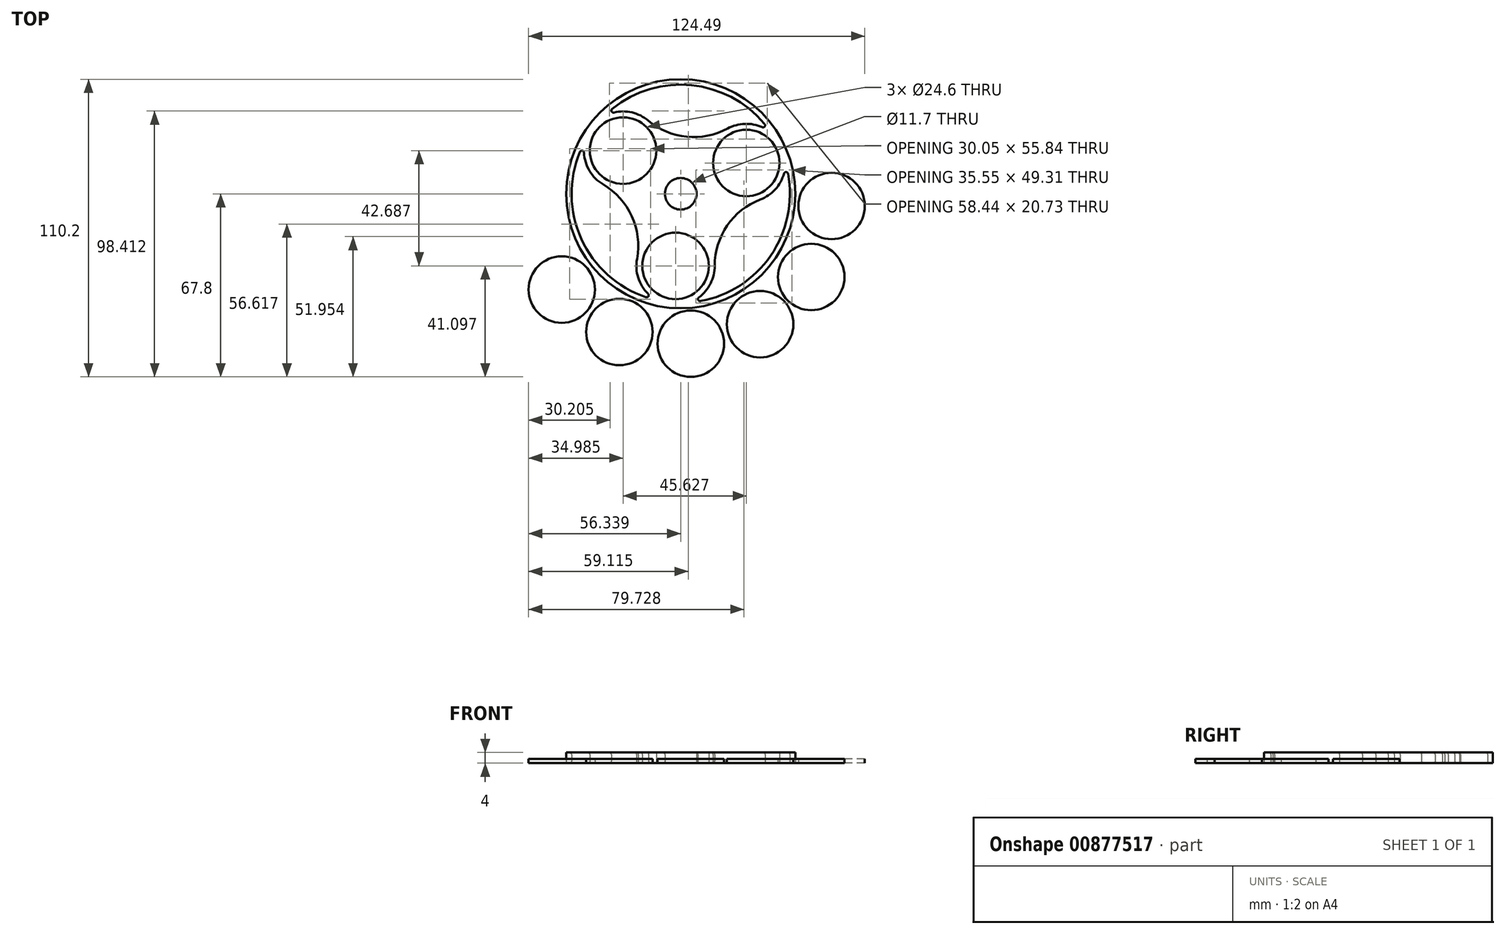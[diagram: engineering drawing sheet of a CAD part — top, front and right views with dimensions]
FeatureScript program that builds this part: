
annotation { "Feature Type Name" : "Feature", "Feature Type Description" : "" }
export const myFeature = defineFeature(function(context is Context, id is Id, definition is map)
    precondition{}
    {
        {
            var Q0;
            Q0=qCreatedBy(makeId("Top.planeOp"),FACE);
            var sketch = newSketch(context, id + "F0", { "sketchPlane" : qUnion([Q0])});
            skCircle(sketch, "E0", {"center": v(-10.22, -0.62) * mm, "radius": 14.5 * mm});
            skCircle(sketch, "E1", {"center": v(15.96, 37.49) * mm, "radius": 14.5 * mm});
            skCircle(sketch, "E2", {"center": v(-29.67, 42.06) * mm, "radius": 14.5 * mm});
            skArc(sketch, "E3", {"start": v(-24.48, 2.04) * mm, "mid": v(-26.4, 17.78) * mm, "end": v(-37, 29.56) * mm});
            skArc(sketch, "E4", {"start": v(21.16, 23.95) * mm, "mid": v(8.9, 14.29) * mm, "end": v(4.28, -0.62) * mm});
            skCircle(sketch, "E5", {"center": v(-29.67, 42.06) * mm, "radius": 12.3 * mm});
            skCircle(sketch, "E6", {"center": v(15.96, 37.49) * mm, "radius": 12.3 * mm});
            skCircle(sketch, "E7", {"center": v(-10.22, -0.62) * mm, "radius": 12.3 * mm});
            skArc(sketch, "E8", {"start": v(-20.36, 53.19) * mm, "mid": v(-6.1, 47.19) * mm, "end": v(9.05, 50.24) * mm});
            skCircle(sketch, "E9", {"center": v(-8.31, 26.08) * mm, "radius": 5.85 * mm});
            skCircle(sketch, "E10", {"center": v(-8.31, 26.08) * mm, "radius": 40.4 * mm});
            skCircle(sketch, "E11", {"center": v(-8.31, 26.08) * mm, "radius": 42.4 * mm});
            skSolve(sketch);
        }
        {
            var Q0;
            {var subQ0=sQuery(id+"F0.wireOp",EDGE,"E3");Q0=makeQuery(id+"F0.imprint","IMPRINT",FACE,{"disambiguationData":[TD([[makeQuery(id+"F0.imprint","IMPRINT",EDGE,{"derivedFrom":subQ0}),-1.0]])]});}
            var Q1;
            Q1=makeQuery(id+"F0.imprint","IMPRINT",FACE,{"disambiguationData":[TD([[makeQuery(id+"F0.imprint","IMPRINT",EDGE,{"derivedFrom":sQuery(id+"F0.wireOp",EDGE,"E5")}),-1.0]])]});
            var Q2;
            Q2=makeQuery(id+"F0.imprint","IMPRINT",FACE,{"disambiguationData":[TD([[makeQuery(id+"F0.imprint","IMPRINT",EDGE,{"derivedFrom":sQuery(id+"F0.wireOp",EDGE,"E6")}),-1.0]])]});
            var Q3;
            Q3=makeQuery(id+"F0.imprint","IMPRINT",FACE,{"disambiguationData":[TD([[makeQuery(id+"F0.imprint","IMPRINT",EDGE,{"derivedFrom":sQuery(id+"F0.wireOp",EDGE,"E7")}),-1.0]])]});
            var Q4;
            Q4=makeQuery(id+"F0.imprint","IMPRINT",FACE,{"disambiguationData":[TD([[makeQuery(id+"F0.imprint","IMPRINT",EDGE,{"derivedFrom":sQuery(id+"F0.wireOp",EDGE,"E11")}),1.0]])]});
            var Q5;
            {var subQ0=sQuery(id+"F0.wireOp",EDGE,"E10");var subQ1=sQuery(id+"F0.wireOp",EDGE,"E1");var subQ2=makeQuery(id+"F0.imprint","INTERSECT",VERTEX,{"disambiguationData":[OD(0.0)],"derivedFrom":[subQ1,subQ0]});Q5=makeQuery(id+"F0.imprint","IMPRINT",FACE,{"disambiguationData":[TD([[makeQuery(id+"F0.imprint","IMPRINT",EDGE,{"disambiguationData":[TD([[subQ2,1.0]])],"derivedFrom":subQ1}),1.0]])]});}
            var Q6;
            {var subQ0=sQuery(id+"F0.wireOp",EDGE,"E10");var subQ1=sQuery(id+"F0.wireOp",EDGE,"E0");var subQ2=makeQuery(id+"F0.imprint","INTERSECT",VERTEX,{"disambiguationData":[OD(0.0)],"derivedFrom":[subQ1,subQ0]});Q6=makeQuery(id+"F0.imprint","IMPRINT",FACE,{"disambiguationData":[TD([[makeQuery(id+"F0.imprint","IMPRINT",EDGE,{"disambiguationData":[TD([[subQ2,-1.0]])],"derivedFrom":subQ1}),1.0]])]});}
            var Q7;
            {var subQ0=sQuery(id+"F0.wireOp",EDGE,"E10");var subQ1=sQuery(id+"F0.wireOp",EDGE,"E2");var subQ2=makeQuery(id+"F0.imprint","INTERSECT",VERTEX,{"disambiguationData":[OD(0.0)],"derivedFrom":[subQ1,subQ0]});Q7=makeQuery(id+"F0.imprint","IMPRINT",FACE,{"disambiguationData":[TD([[makeQuery(id+"F0.imprint","IMPRINT",EDGE,{"disambiguationData":[TD([[subQ2,-1.0]])],"derivedFrom":subQ1}),1.0]])]});}
            extrude(context, id + "F1", {"entities" : qUnion([Q0, Q1, Q2, Q3, Q4, Q5, Q6, Q7]), "depth" : 4 * mm, "offsetDistance" : 25.4 * mm});
        }
        {
            var Q0;
            Q0=makeQuery(id+"F1.opExtrude","SWEPT_FACE",FACE,{"disambiguationData":[OSD([sQuery(id+"F0.wireOp",EDGE,"E9")])]});
            var Q1;
            Q1=makeQuery(id+"F1.opExtrude","CAP_EDGE",EDGE,{"disambiguationData":[OSD([sQuery(id+"F0.wireOp",EDGE,"E9")])],"isStart":true});
            var Q2;
            {var subQ0=sQuery(id+"F0.wireOp",EDGE,"E10");Q2=makeQuery(id+"F1.opExtrude","SWEPT_FACE",FACE,{"disambiguationData":[OSD([subQ0]),TDD([makeQuery(id+"F0.imprint","IMPRINT",EDGE,{"disambiguationData":[TD([[makeQuery(id+"F0.imprint","INTERSECT",VERTEX,{"disambiguationData":[OD(0.0)],"derivedFrom":[sQuery(id+"F0.wireOp",EDGE,"E0"),subQ0]}),1.0]])],"derivedFrom":subQ0})])]});}
            var Q3;
            {var subQ0=sQuery(id+"F0.wireOp",EDGE,"E10");Q3=makeQuery(id+"F1.opExtrude","SWEPT_FACE",FACE,{"disambiguationData":[OSD([subQ0]),TDD([makeQuery(id+"F0.imprint","IMPRINT",EDGE,{"disambiguationData":[TD([[makeQuery(id+"F0.imprint","INTERSECT",VERTEX,{"disambiguationData":[OD(1.0)],"derivedFrom":[sQuery(id+"F0.wireOp",EDGE,"E0"),subQ0]}),-1.0]])],"derivedFrom":subQ0})])]});}
            var Q4;
            {var subQ0=sQuery(id+"F0.wireOp",EDGE,"E10");Q4=makeQuery(id+"F1.opExtrude","SWEPT_FACE",FACE,{"disambiguationData":[OSD([subQ0]),TDD([makeQuery(id+"F0.imprint","IMPRINT",EDGE,{"disambiguationData":[TD([[makeQuery(id+"F0.imprint","INTERSECT",VERTEX,{"disambiguationData":[OD(0.0)],"derivedFrom":[sQuery(id+"F0.wireOp",EDGE,"E1"),subQ0]}),-1.0]])],"derivedFrom":subQ0})])]});}
            var Q5;
            Q5=makeQuery(id+"F1.opExtrude","CAP_EDGE",EDGE,{"disambiguationData":[OSD([sQuery(id+"F0.wireOp",EDGE,"E9")])],"isStart":false});
            var Q6;
            Q6=makeQuery(id+"F1.opExtrude","CAP_EDGE",EDGE,{"disambiguationData":[OSD([sQuery(id+"F0.wireOp",EDGE,"E8")])],"isStart":true});
            var Q7;
            {var subQ0=sQuery(id+"F0.wireOp",EDGE,"E10");Q7=makeQuery(id+"F1.opExtrude","CAP_EDGE",EDGE,{"disambiguationData":[OSD([subQ0]),TDD([makeQuery(id+"F0.imprint","IMPRINT",EDGE,{"disambiguationData":[TD([[makeQuery(id+"F0.imprint","INTERSECT",VERTEX,{"disambiguationData":[OD(0.0)],"derivedFrom":[sQuery(id+"F0.wireOp",EDGE,"E0"),subQ0]}),1.0]])],"derivedFrom":subQ0})])],"isStart":false});}
            var Q8;
            Q8=makeQuery(id+"F1.opExtrude","CAP_EDGE",EDGE,{"disambiguationData":[OSD([sQuery(id+"F0.wireOp",EDGE,"E8")])],"isStart":false});
            var Q9;
            {var subQ0=sQuery(id+"F0.wireOp",EDGE,"E10");Q9=makeQuery(id+"F1.opExtrude","CAP_EDGE",EDGE,{"disambiguationData":[OSD([subQ0]),TDD([makeQuery(id+"F0.imprint","IMPRINT",EDGE,{"disambiguationData":[TD([[makeQuery(id+"F0.imprint","INTERSECT",VERTEX,{"disambiguationData":[OD(0.0)],"derivedFrom":[sQuery(id+"F0.wireOp",EDGE,"E1"),subQ0]}),-1.0]])],"derivedFrom":subQ0})])],"isStart":false});}
            var Q10;
            Q10=makeQuery(id+"F1.opExtrude","CAP_EDGE",EDGE,{"disambiguationData":[OSD([sQuery(id+"F0.wireOp",EDGE,"E4")])],"isStart":false});
            var Q11;
            {var subQ0=sQuery(id+"F0.wireOp",EDGE,"E10");Q11=makeQuery(id+"F1.opExtrude","CAP_EDGE",EDGE,{"disambiguationData":[OSD([subQ0]),TDD([makeQuery(id+"F0.imprint","IMPRINT",EDGE,{"disambiguationData":[TD([[makeQuery(id+"F0.imprint","INTERSECT",VERTEX,{"disambiguationData":[OD(0.0)],"derivedFrom":[sQuery(id+"F0.wireOp",EDGE,"E0"),subQ0]}),1.0]])],"derivedFrom":subQ0})])],"isStart":true});}
            var Q12;
            {var subQ0=sQuery(id+"F0.wireOp",EDGE,"E10");Q12=makeQuery(id+"F1.opExtrude","CAP_EDGE",EDGE,{"disambiguationData":[OSD([subQ0]),TDD([makeQuery(id+"F0.imprint","IMPRINT",EDGE,{"disambiguationData":[TD([[makeQuery(id+"F0.imprint","INTERSECT",VERTEX,{"disambiguationData":[OD(1.0)],"derivedFrom":[sQuery(id+"F0.wireOp",EDGE,"E0"),subQ0]}),-1.0]])],"derivedFrom":subQ0})])],"isStart":true});}
            var Q13;
            {var subQ0=sQuery(id+"F0.wireOp",EDGE,"E10");Q13=makeQuery(id+"F1.opExtrude","CAP_EDGE",EDGE,{"disambiguationData":[OSD([subQ0]),TDD([makeQuery(id+"F0.imprint","IMPRINT",EDGE,{"disambiguationData":[TD([[makeQuery(id+"F0.imprint","INTERSECT",VERTEX,{"disambiguationData":[OD(1.0)],"derivedFrom":[sQuery(id+"F0.wireOp",EDGE,"E0"),subQ0]}),-1.0]])],"derivedFrom":subQ0})])],"isStart":false});}
            var Q14;
            {var subQ0=sQuery(id+"F0.wireOp",EDGE,"E1");Q14=makeQuery(id+"F1.opExtrude","CAP_EDGE",EDGE,{"disambiguationData":[OSD([subQ0]),TDD([makeQuery(id+"F0.imprint","IMPRINT",EDGE,{"disambiguationData":[TD([[makeQuery(id+"F0.imprint","INTERSECT",VERTEX,{"derivedFrom":[subQ0,sQuery(id+"F0.wireOp",EDGE,"E4")]}),-1.0]])],"derivedFrom":subQ0})])],"isStart":false});}
            var Q15;
            Q15=makeQuery(id+"F1.opExtrude","SWEPT_EDGE",EDGE,{"disambiguationData":[OSD([sQuery(id+"F0.wireOp",EDGE,"E1"),sQuery(id+"F0.wireOp",EDGE,"E4")])]});
            var Q16;
            Q16=makeQuery(id+"F1.opExtrude","CAP_EDGE",EDGE,{"disambiguationData":[OSD([sQuery(id+"F0.wireOp",EDGE,"E9")])],"isStart":false});
            var Q17;
            {var subQ0=sQuery(id+"F0.wireOp",EDGE,"E2");Q17=makeQuery(id+"F1.opExtrude","CAP_EDGE",EDGE,{"disambiguationData":[OSD([subQ0]),TDD([makeQuery(id+"F0.imprint","IMPRINT",EDGE,{"disambiguationData":[TD([[makeQuery(id+"F0.imprint","INTERSECT",VERTEX,{"derivedFrom":[subQ0,sQuery(id+"F0.wireOp",EDGE,"E3")]}),1.0]])],"derivedFrom":subQ0})])],"isStart":true});}
            var Q18;
            Q18=makeQuery(id+"F1.opExtrude","SWEPT_EDGE",EDGE,{"disambiguationData":[OSD([sQuery(id+"F0.wireOp",EDGE,"E1"),sQuery(id+"F0.wireOp",EDGE,"E8")])]});
            var Q19;
            {var subQ0=sQuery(id+"F0.wireOp",EDGE,"E0");Q19=makeQuery(id+"F1.opExtrude","CAP_EDGE",EDGE,{"disambiguationData":[OSD([subQ0]),TDD([makeQuery(id+"F0.imprint","IMPRINT",EDGE,{"disambiguationData":[TD([[makeQuery(id+"F0.imprint","INTERSECT",VERTEX,{"derivedFrom":[subQ0,sQuery(id+"F0.wireOp",EDGE,"E3")]}),-1.0]])],"derivedFrom":subQ0})])],"isStart":true});}
            var Q20;
            Q20=makeQuery(id+"F1.opExtrude","SWEPT_EDGE",EDGE,{"disambiguationData":[OSD([sQuery(id+"F0.wireOp",EDGE,"E0"),sQuery(id+"F0.wireOp",EDGE,"E3")])]});
            var Q21;
            Q21=makeQuery(id+"F1.opExtrude","CAP_EDGE",EDGE,{"disambiguationData":[OSD([sQuery(id+"F0.wireOp",EDGE,"E6")])],"isStart":true});
            var Q22;
            {var subQ0=sQuery(id+"F0.wireOp",EDGE,"E1");Q22=makeQuery(id+"F1.opExtrude","CAP_EDGE",EDGE,{"disambiguationData":[OSD([subQ0]),TDD([makeQuery(id+"F0.imprint","IMPRINT",EDGE,{"disambiguationData":[TD([[makeQuery(id+"F0.imprint","INTERSECT",VERTEX,{"derivedFrom":[subQ0,sQuery(id+"F0.wireOp",EDGE,"E8")]}),1.0]])],"derivedFrom":subQ0})])],"isStart":false});}
            var Q23;
            {var subQ0=sQuery(id+"F0.wireOp",EDGE,"E1");Q23=makeQuery(id+"F1.opExtrude","CAP_EDGE",EDGE,{"disambiguationData":[OSD([subQ0]),TDD([makeQuery(id+"F0.imprint","IMPRINT",EDGE,{"disambiguationData":[TD([[makeQuery(id+"F0.imprint","INTERSECT",VERTEX,{"derivedFrom":[subQ0,sQuery(id+"F0.wireOp",EDGE,"E4")]}),-1.0]])],"derivedFrom":subQ0})])],"isStart":true});}
            var Q24;
            {var subQ0=sQuery(id+"F0.wireOp",EDGE,"E0");Q24=makeQuery(id+"F1.opExtrude","CAP_EDGE",EDGE,{"disambiguationData":[OSD([subQ0]),TDD([makeQuery(id+"F0.imprint","IMPRINT",EDGE,{"disambiguationData":[TD([[makeQuery(id+"F0.imprint","INTERSECT",VERTEX,{"derivedFrom":[subQ0,sQuery(id+"F0.wireOp",EDGE,"E4")]}),1.0]])],"derivedFrom":subQ0})])],"isStart":false});}
            var Q25;
            Q25=makeQuery(id+"F1.opExtrude","CAP_EDGE",EDGE,{"disambiguationData":[OSD([sQuery(id+"F0.wireOp",EDGE,"E7")])],"isStart":true});
            var Q26;
            Q26=makeQuery(id+"F1.opExtrude","CAP_EDGE",EDGE,{"disambiguationData":[OSD([sQuery(id+"F0.wireOp",EDGE,"E7")])],"isStart":false});
            var Q27;
            {var subQ0=sQuery(id+"F0.wireOp",EDGE,"E10");var subQ1=sQuery(id+"F0.wireOp",EDGE,"E2");Q27=makeQuery(id+"F1.opExtrude","SWEPT_EDGE",EDGE,{"disambiguationData":[OSD([subQ1,subQ0]),TDD([makeQuery(id+"F0.imprint","INTERSECT",VERTEX,{"disambiguationData":[OD(0.0)],"derivedFrom":[subQ1,subQ0]})])]});}
            var Q28;
            {var subQ0=sQuery(id+"F0.wireOp",EDGE,"E10");var subQ1=sQuery(id+"F0.wireOp",EDGE,"E2");Q28=makeQuery(id+"F1.opExtrude","SWEPT_EDGE",EDGE,{"disambiguationData":[OSD([subQ1,subQ0]),TDD([makeQuery(id+"F0.imprint","INTERSECT",VERTEX,{"disambiguationData":[OD(1.0)],"derivedFrom":[subQ1,subQ0]})])]});}
            var Q29;
            {var subQ0=sQuery(id+"F0.wireOp",EDGE,"E2");Q29=makeQuery(id+"F1.opExtrude","CAP_EDGE",EDGE,{"disambiguationData":[OSD([subQ0]),TDD([makeQuery(id+"F0.imprint","IMPRINT",EDGE,{"disambiguationData":[TD([[makeQuery(id+"F0.imprint","INTERSECT",VERTEX,{"derivedFrom":[subQ0,sQuery(id+"F0.wireOp",EDGE,"E8")]}),-1.0]])],"derivedFrom":subQ0})])],"isStart":true});}
            var Q30;
            Q30=makeQuery(id+"F1.opExtrude","CAP_EDGE",EDGE,{"disambiguationData":[OSD([sQuery(id+"F0.wireOp",EDGE,"E5")])],"isStart":true});
            var Q31;
            Q31=makeQuery(id+"F1.opExtrude","CAP_EDGE",EDGE,{"disambiguationData":[OSD([sQuery(id+"F0.wireOp",EDGE,"E5")])],"isStart":false});
            var Q32;
            {var subQ0=sQuery(id+"F0.wireOp",EDGE,"E2");Q32=makeQuery(id+"F1.opExtrude","CAP_EDGE",EDGE,{"disambiguationData":[OSD([subQ0]),TDD([makeQuery(id+"F0.imprint","IMPRINT",EDGE,{"disambiguationData":[TD([[makeQuery(id+"F0.imprint","INTERSECT",VERTEX,{"derivedFrom":[subQ0,sQuery(id+"F0.wireOp",EDGE,"E3")]}),1.0]])],"derivedFrom":subQ0})])],"isStart":false});}
            var Q33;
            {var subQ0=sQuery(id+"F0.wireOp",EDGE,"E10");Q33=makeQuery(id+"F1.opExtrude","CAP_EDGE",EDGE,{"disambiguationData":[OSD([subQ0]),TDD([makeQuery(id+"F0.imprint","IMPRINT",EDGE,{"disambiguationData":[TD([[makeQuery(id+"F0.imprint","INTERSECT",VERTEX,{"disambiguationData":[OD(0.0)],"derivedFrom":[sQuery(id+"F0.wireOp",EDGE,"E1"),subQ0]}),-1.0]])],"derivedFrom":subQ0})])],"isStart":true});}
            var Q34;
            Q34=makeQuery(id+"F1.opExtrude","SWEPT_EDGE",EDGE,{"disambiguationData":[OSD([sQuery(id+"F0.wireOp",EDGE,"E2"),sQuery(id+"F0.wireOp",EDGE,"E3")])]});
            var Q35;
            {var subQ0=sQuery(id+"F0.wireOp",EDGE,"E0");Q35=makeQuery(id+"F1.opExtrude","CAP_EDGE",EDGE,{"disambiguationData":[OSD([subQ0]),TDD([makeQuery(id+"F0.imprint","IMPRINT",EDGE,{"disambiguationData":[TD([[makeQuery(id+"F0.imprint","INTERSECT",VERTEX,{"derivedFrom":[subQ0,sQuery(id+"F0.wireOp",EDGE,"E4")]}),1.0]])],"derivedFrom":subQ0})])],"isStart":true});}
            var Q36;
            Q36=makeQuery(id+"F1.opExtrude","CAP_EDGE",EDGE,{"disambiguationData":[OSD([sQuery(id+"F0.wireOp",EDGE,"E3")])],"isStart":false});
            var Q37;
            {var subQ0=sQuery(id+"F0.wireOp",EDGE,"E1");Q37=makeQuery(id+"F1.opExtrude","CAP_EDGE",EDGE,{"disambiguationData":[OSD([subQ0]),TDD([makeQuery(id+"F0.imprint","IMPRINT",EDGE,{"disambiguationData":[TD([[makeQuery(id+"F0.imprint","INTERSECT",VERTEX,{"derivedFrom":[subQ0,sQuery(id+"F0.wireOp",EDGE,"E8")]}),1.0]])],"derivedFrom":subQ0})])],"isStart":true});}
            var Q38;
            {var subQ0=sQuery(id+"F0.wireOp",EDGE,"E10");var subQ1=sQuery(id+"F0.wireOp",EDGE,"E1");Q38=makeQuery(id+"F1.opExtrude","SWEPT_EDGE",EDGE,{"disambiguationData":[OSD([subQ1,subQ0]),TDD([makeQuery(id+"F0.imprint","INTERSECT",VERTEX,{"disambiguationData":[OD(1.0)],"derivedFrom":[subQ1,subQ0]})])]});}
            var Q39;
            {var subQ0=sQuery(id+"F0.wireOp",EDGE,"E2");Q39=makeQuery(id+"F1.opExtrude","CAP_EDGE",EDGE,{"disambiguationData":[OSD([subQ0]),TDD([makeQuery(id+"F0.imprint","IMPRINT",EDGE,{"disambiguationData":[TD([[makeQuery(id+"F0.imprint","INTERSECT",VERTEX,{"derivedFrom":[subQ0,sQuery(id+"F0.wireOp",EDGE,"E8")]}),-1.0]])],"derivedFrom":subQ0})])],"isStart":false});}
            var Q40;
            Q40=makeQuery(id+"F1.opExtrude","CAP_EDGE",EDGE,{"disambiguationData":[OSD([sQuery(id+"F0.wireOp",EDGE,"E9")])],"isStart":true});
            var Q41;
            Q41=makeQuery(id+"F1.opExtrude","CAP_EDGE",EDGE,{"disambiguationData":[OSD([sQuery(id+"F0.wireOp",EDGE,"E3")])],"isStart":true});
            var Q42;
            Q42=makeQuery(id+"F1.opExtrude","CAP_EDGE",EDGE,{"disambiguationData":[OSD([sQuery(id+"F0.wireOp",EDGE,"E6")])],"isStart":false});
            var Q43;
            Q43=makeQuery(id+"F1.opExtrude","CAP_EDGE",EDGE,{"disambiguationData":[OSD([sQuery(id+"F0.wireOp",EDGE,"E4")])],"isStart":true});
            var Q44;
            {var subQ0=sQuery(id+"F0.wireOp",EDGE,"E0");Q44=makeQuery(id+"F1.opExtrude","CAP_EDGE",EDGE,{"disambiguationData":[OSD([subQ0]),TDD([makeQuery(id+"F0.imprint","IMPRINT",EDGE,{"disambiguationData":[TD([[makeQuery(id+"F0.imprint","INTERSECT",VERTEX,{"derivedFrom":[subQ0,sQuery(id+"F0.wireOp",EDGE,"E3")]}),-1.0]])],"derivedFrom":subQ0})])],"isStart":false});}
            var Q45;
            {var subQ0=sQuery(id+"F0.wireOp",EDGE,"E10");var subQ1=sQuery(id+"F0.wireOp",EDGE,"E1");Q45=makeQuery(id+"F1.opExtrude","SWEPT_EDGE",EDGE,{"disambiguationData":[OSD([subQ1,subQ0]),TDD([makeQuery(id+"F0.imprint","INTERSECT",VERTEX,{"disambiguationData":[OD(0.0)],"derivedFrom":[subQ1,subQ0]})])]});}
            var Q46;
            {var subQ0=sQuery(id+"F0.wireOp",EDGE,"E10");var subQ1=sQuery(id+"F0.wireOp",EDGE,"E0");Q46=makeQuery(id+"F1.opExtrude","SWEPT_EDGE",EDGE,{"disambiguationData":[OSD([subQ1,subQ0]),TDD([makeQuery(id+"F0.imprint","INTERSECT",VERTEX,{"disambiguationData":[OD(1.0)],"derivedFrom":[subQ1,subQ0]})])]});}
            var Q47;
            Q47=makeQuery(id+"F1.opExtrude","SWEPT_EDGE",EDGE,{"disambiguationData":[OSD([sQuery(id+"F0.wireOp",EDGE,"E0"),sQuery(id+"F0.wireOp",EDGE,"E4")])]});
            var Q48;
            {var subQ0=sQuery(id+"F0.wireOp",EDGE,"E10");var subQ1=sQuery(id+"F0.wireOp",EDGE,"E0");Q48=makeQuery(id+"F1.opExtrude","SWEPT_EDGE",EDGE,{"disambiguationData":[OSD([subQ1,subQ0]),TDD([makeQuery(id+"F0.imprint","INTERSECT",VERTEX,{"disambiguationData":[OD(0.0)],"derivedFrom":[subQ1,subQ0]})])]});}
            var Q49;
            Q49=makeQuery(id+"F1.opExtrude","SWEPT_EDGE",EDGE,{"disambiguationData":[OSD([sQuery(id+"F0.wireOp",EDGE,"E2"),sQuery(id+"F0.wireOp",EDGE,"E8")])]});
            fillet(context, id + "F2", {"entities" : qUnion([Q0, Q1, Q2, Q3, Q4, Q5, Q6, Q7, Q8, Q9, Q10, Q11, Q12, Q13, Q14, Q15, Q16, Q17, Q18, Q19, Q20, Q21, Q22, Q23, Q24, Q25, Q26, Q27, Q28, Q29, Q30, Q31, Q32, Q33, Q34, Q35, Q36, Q37, Q38, Q39, Q40, Q41, Q42, Q43, Q44, Q45, Q46, Q47, Q48, Q49]), "radius" : 0.76 * mm, "tangentPropagation" : true, "allowEdgeOverflow" : false});
        }
        {
            var Q0;
            Q0=qCreatedBy(makeId("Top.planeOp"),FACE);
            var sketch = newSketch(context, id + "F3", { "sketchPlane" : qUnion([Q0])});
            skCircle(sketch, "E12", {"center": v(-4.57, -29.42) * mm, "radius": 12.3 * mm});
            skCircle(sketch, "E13", {"center": v(21.08, -22.2) * mm, "radius": 12.3 * mm});
            skCircle(sketch, "E14", {"center": v(40, -4.73) * mm, "radius": 12.3 * mm});
            skCircle(sketch, "E15", {"center": v(-52.35, -9.38) * mm, "radius": 12.3 * mm});
            skCircle(sketch, "E16", {"center": v(-31.03, -25.1) * mm, "radius": 12.3 * mm});
            skCircle(sketch, "E17", {"center": v(47.54, 21.56) * mm, "radius": 12.3 * mm});
            skSolve(sketch);
        }
        {
            var Q0;
            Q0 = qSketchRegion(id + "F3", true);
            extrude(context, id + "F4", {"entities" : qUnion([Q0]), "depth" : 1.6 * mm, "offsetDistance" : 25.4 * mm});
        }
    });
